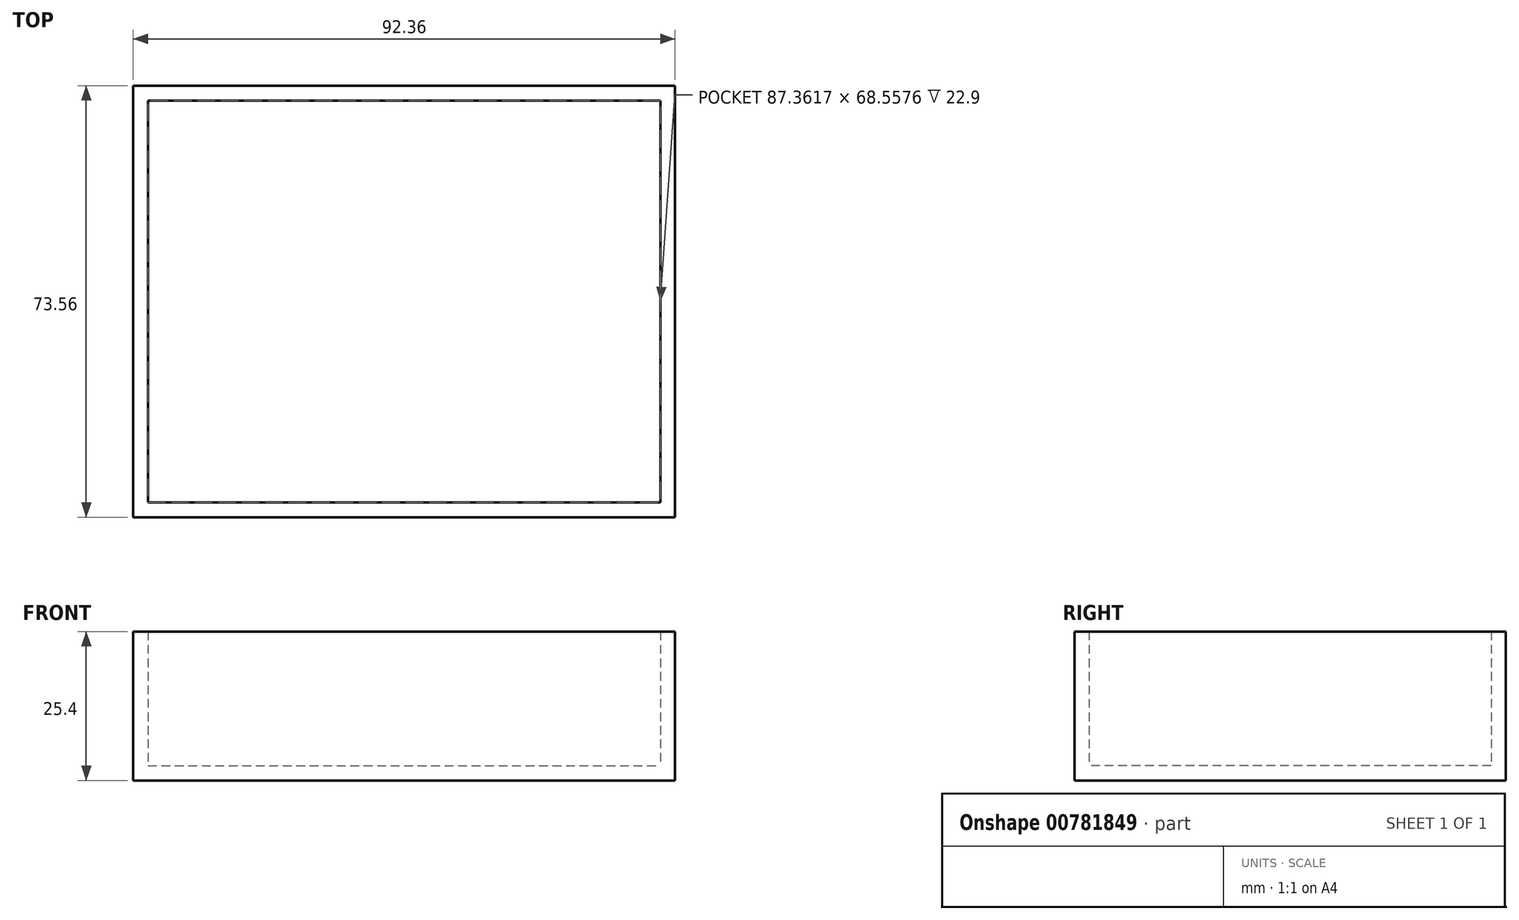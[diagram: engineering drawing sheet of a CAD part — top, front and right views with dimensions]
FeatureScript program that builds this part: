
annotation { "Feature Type Name" : "Feature", "Feature Type Description" : "" }
export const myFeature = defineFeature(function(context is Context, id is Id, definition is map)
    precondition{}
    {
        {
            var Q0;
            Q0=qCreatedBy(makeId("Top.planeOp"),FACE);
            var sketch = newSketch(context, id + "F0", { "sketchPlane" : qUnion([Q0])});
            skPoint(sketch, "E0.0", {"position": v(0, 0) * mm});
            skLineSegment(sketch, "E1.bottom", {"start": v(-44.34, 41.76) * mm, "end": v(48.02, 41.76) * mm});
            skLineSegment(sketch, "E1.top", {"start": v(-44.34, -31.8) * mm, "end": v(48.02, -31.8) * mm});
            skLineSegment(sketch, "E1.left", {"start": v(-44.34, 41.76) * mm, "end": v(-44.34, -31.8) * mm});
            skLineSegment(sketch, "E1.right", {"start": v(48.02, 41.76) * mm, "end": v(48.02, -31.8) * mm});
            skSolve(sketch);
        }
        {
            var Q0;
            Q0=makeQuery(id+"F0.imprint","IMPRINT",FACE,{"disambiguationData":[TD([[makeQuery(id+"F0.imprint","IMPRINT",EDGE,{"derivedFrom":sQuery(id+"F0.wireOp",EDGE,"E1.bottom")}),-1.0]])]});
            extrude(context, id + "F1", {"entities" : qUnion([Q0]), "depth" : 25.4 * mm, "offsetDistance" : 25.4 * mm});
        }
        {
            var Q0;
            Q0=makeQuery(id+"F0.imprint","IMPRINT",FACE,{"disambiguationData":[TD([[makeQuery(id+"F0.imprint","IMPRINT",EDGE,{"derivedFrom":sQuery(id+"F0.wireOp",EDGE,"E1.bottom")}),-1.0]])]});
            extrude(context, id + "F2", {"entities" : qUnion([Q0]), "operationType" : NewBodyOperationType.ADD, "depth" : 25 * mm, "offsetDistance" : 25 * mm});
        }
        {
            var Q0;
            Q0=makeQuery(id+"F1.opExtrude","CAP_FACE",FACE,{"disambiguationData":[OSD([sQuery(id+"F0.wireOp",EDGE,"E1.bottom"),sQuery(id+"F0.wireOp",EDGE,"E1.top"),sQuery(id+"F0.wireOp",EDGE,"E1.left"),sQuery(id+"F0.wireOp",EDGE,"E1.right")])],"isStart":false});
            shell(context, id + "F3", {"entities" : qUnion([Q0]), "thickness" : 2.5 * mm});
        }
        {
            var Q1;
            Q1=makeQuery(id+"F3.opShell","OFFSET_FACE",FACE,{"disambiguationData":[OSD([sQuery(id+"F0.wireOp",EDGE,"E1.bottom"),sQuery(id+"F0.wireOp",EDGE,"E1.top"),sQuery(id+"F0.wireOp",EDGE,"E1.left"),sQuery(id+"F0.wireOp",EDGE,"E1.right")])]});
            var Q2;
            Q2=qCreatedBy(makeId("Origin.pointOp"),VERTEX);
            loft(context, id + "F4", {"operationType" : NewBodyOperationType.ADD, "sheetProfilesArray" : [{ "sheetProfileEntities" : qUnion([Q1]) }, { "sheetProfileEntities" : qUnion([Q2]) }]});
        }
    });
